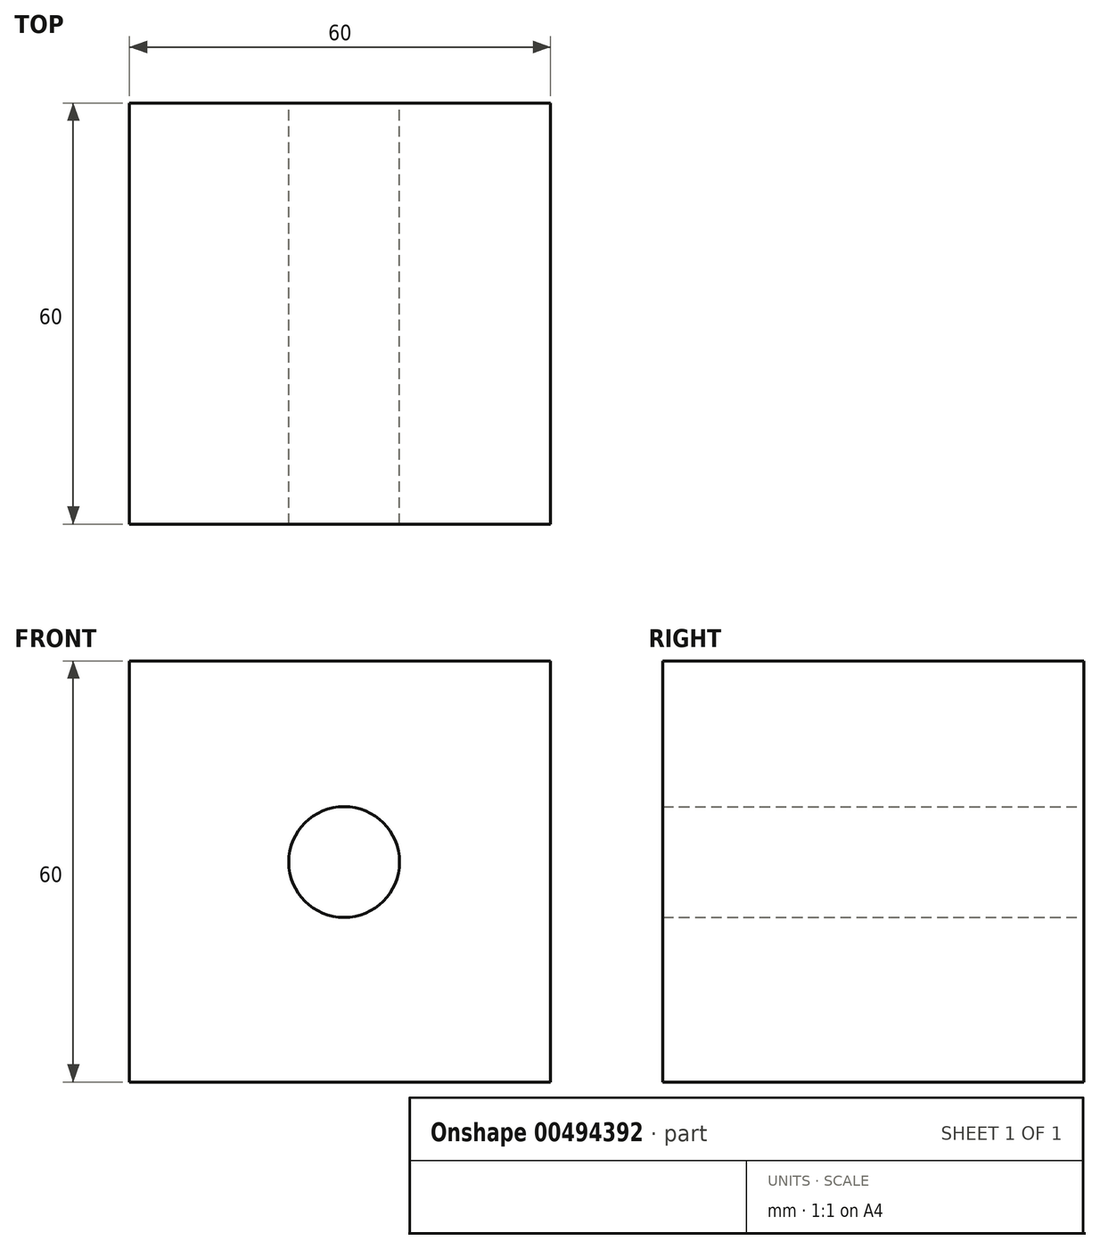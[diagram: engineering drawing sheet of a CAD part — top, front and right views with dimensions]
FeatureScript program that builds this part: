
annotation { "Feature Type Name" : "Feature", "Feature Type Description" : "" }
export const myFeature = defineFeature(function(context is Context, id is Id, definition is map)
    precondition{}
    {
        {
            var Q0;
            Q0=qCreatedBy(makeId("Front.planeOp"),FACE);
            var sketch = newSketch(context, id + "F0", { "sketchPlane" : qUnion([Q0])});
            skLineSegment(sketch, "E0.bottom", {"start": v(-57.96, -39.26) * mm, "end": v(2.04, -39.26) * mm});
            skLineSegment(sketch, "E0.top", {"start": v(-57.96, 20.74) * mm, "end": v(2.04, 20.74) * mm});
            skLineSegment(sketch, "E0.left", {"start": v(-57.96, -39.26) * mm, "end": v(-57.96, 20.74) * mm});
            skLineSegment(sketch, "E0.right", {"start": v(2.04, -39.26) * mm, "end": v(2.04, 20.74) * mm});
            skCircle(sketch, "E1", {"center": v(-27.37, -7.92) * mm, "radius": 7.9 * mm});
            skSolve(sketch);
        }
        {
            var Q0;
            Q0 = qSketchRegion(id + "F0", true);
            extrude(context, id + "F1", {"entities" : qUnion([Q0]), "depth" : 60 * mm});
        }
    });
